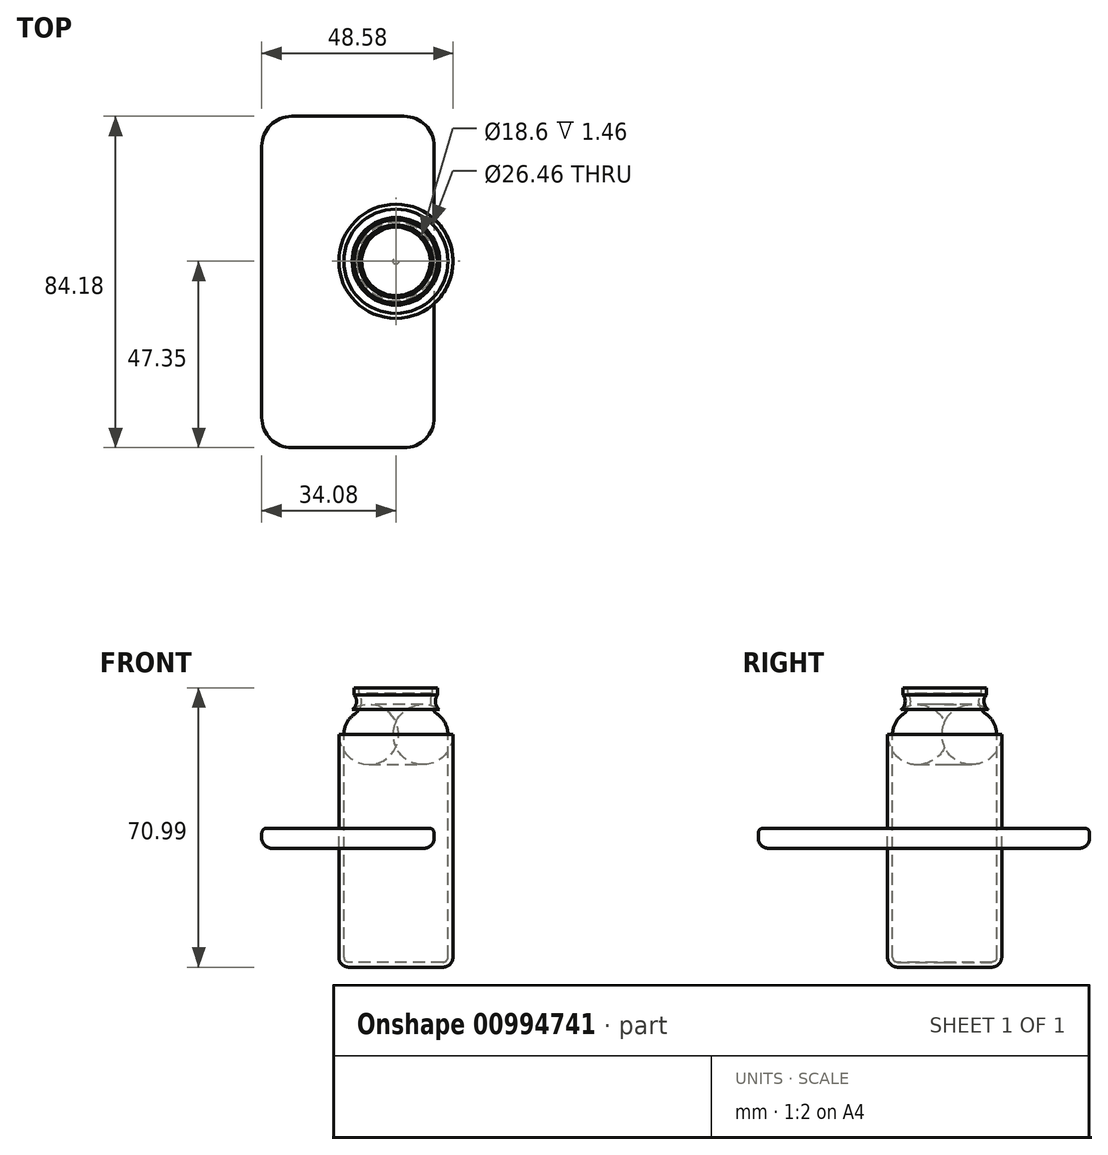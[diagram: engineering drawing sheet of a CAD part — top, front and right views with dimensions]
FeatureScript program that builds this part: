
annotation { "Feature Type Name" : "Feature", "Feature Type Description" : "" }
export const myFeature = defineFeature(function(context is Context, id is Id, definition is map)
    precondition{}
    {
        {
            var Q0;
            Q0=qCreatedBy(makeId("Top.planeOp"),FACE);
            var sketch = newSketch(context, id + "F0", { "sketchPlane" : qUnion([Q0])});
            skLineSegment(sketch, "E0.bottom", {"start": v(-34.08, 36.83) * mm, "end": v(9.72, 36.83) * mm});
            skLineSegment(sketch, "E0.top", {"start": v(-34.08, -47.35) * mm, "end": v(9.72, -47.35) * mm});
            skLineSegment(sketch, "E0.left", {"start": v(-34.08, 36.83) * mm, "end": v(-34.08, -47.35) * mm});
            skLineSegment(sketch, "E0.right", {"start": v(9.72, 36.83) * mm, "end": v(9.72, -47.35) * mm});
            skSolve(sketch);
        }
        {
            var Q0;
            Q0=makeQuery(id+"F0.imprint","IMPRINT",FACE,{"disambiguationData":[TD([[makeQuery(id+"F0.imprint","IMPRINT",EDGE,{"derivedFrom":sQuery(id+"F0.wireOp",EDGE,"E0.bottom")}),-1.0]])]});
            extrude(context, id + "F1", {"entities" : qUnion([Q0]), "depth" : 5.08 * mm, "offsetDistance" : 25.4 * mm});
        }
        {
            var Q0;
            Q0=makeQuery(id+"F1.opExtrude","SWEPT_EDGE",EDGE,{"disambiguationData":[OSD([sQuery(id+"F0.wireOp",EDGE,"E0.top"),sQuery(id+"F0.wireOp",EDGE,"E0.left")])]});
            var Q1;
            Q1=makeQuery(id+"F1.opExtrude","SWEPT_EDGE",EDGE,{"disambiguationData":[OSD([sQuery(id+"F0.wireOp",EDGE,"E0.top"),sQuery(id+"F0.wireOp",EDGE,"E0.right")])]});
            var Q2;
            Q2=makeQuery(id+"F1.opExtrude","SWEPT_EDGE",EDGE,{"disambiguationData":[OSD([sQuery(id+"F0.wireOp",EDGE,"E0.bottom"),sQuery(id+"F0.wireOp",EDGE,"E0.right")])]});
            var Q3;
            Q3=makeQuery(id+"F1.opExtrude","SWEPT_EDGE",EDGE,{"disambiguationData":[OSD([sQuery(id+"F0.wireOp",EDGE,"E0.bottom"),sQuery(id+"F0.wireOp",EDGE,"E0.left")])]});
            fillet(context, id + "F2", {"entities" : qUnion([Q0, Q1, Q2, Q3]), "radius" : 7.62 * mm, "tangentPropagation" : true, "allowEdgeOverflow" : false});
        }
        {
            var Q0;
            Q0=makeQuery(id+"F1.opExtrude","CAP_EDGE",EDGE,{"disambiguationData":[OSD([sQuery(id+"F0.wireOp",EDGE,"E0.left")])],"isStart":true});
            fillet(context, id + "F3", {"entities" : qUnion([Q0]), "radius" : 2.54 * mm, "tangentPropagation" : true, "allowEdgeOverflow" : false});
        }
        {
            var Q0;
            Q0=makeQuery(id+"F1.opExtrude","CAP_EDGE",EDGE,{"disambiguationData":[OSD([sQuery(id+"F0.wireOp",EDGE,"E0.left")])],"isStart":false});
            fillet(context, id + "F4", {"entities" : qUnion([Q0]), "radius" : 1.27 * mm, "tangentPropagation" : true, "allowEdgeOverflow" : false});
        }
        {
            var Q0;
            Q0=qCreatedBy(makeId("Front.planeOp"),FACE);
            var sketch = newSketch(context, id + "F5", { "sketchPlane" : qUnion([Q0])});
            skLineSegment(sketch, "E1.top", {"start": v(0, -30.22) * mm, "end": v(14.5, -30.22) * mm});
            skLineSegment(sketch, "E1.left", {"start": v(0, 32.43) * mm, "end": v(0, -30.22) * mm});
            skLineSegment(sketch, "E1.right", {"start": v(14.5, 33.28) * mm, "end": v(14.5, -30.22) * mm});
            skLineSegment(sketch, "E2", {"start": v(14.5, 33.28) * mm, "end": v(9.09, 36.4) * mm});
            skLineSegment(sketch, "E3", {"start": v(9.09, 36.4) * mm, "end": v(10.57, 38.97) * mm});
            skLineSegment(sketch, "E4", {"start": v(10.57, 38.97) * mm, "end": v(10.57, 40.77) * mm});
            skLineSegment(sketch, "E5", {"start": v(10.57, 40.77) * mm, "end": v(0, 40.77) * mm});
            skLineSegment(sketch, "E6", {"start": v(0, 40.77) * mm, "end": v(0, 32.43) * mm});
            skSolve(sketch);
        }
        {
            var Q0;
            Q0=makeQuery(id+"F5.imprint","IMPRINT",FACE,{"disambiguationData":[TD([[makeQuery(id+"F5.imprint","IMPRINT",EDGE,{"derivedFrom":sQuery(id+"F5.wireOp",EDGE,"E1.top")}),1.0]])]});
            var Q1;
            Q1=sQuery(id+"F5.wireOp",EDGE,"E1.left");
            revolve(context, id + "F6", {"surfaceOperationType" : NewSurfaceOperationType.NEW, "entities" : qUnion([Q0]), "axis" : qUnion([Q1]), "revolveType" : RevolveType.FULL});
        }
        {
            var Q0;
            Q0=makeQuery(id+"F6.opRevolve","SWEPT_EDGE",EDGE,{"disambiguationData":[OSD([sQuery(id+"F5.wireOp",EDGE,"E1.top"),sQuery(id+"F5.wireOp",EDGE,"E1.right")])]});
            fillet(context, id + "F7", {"entities" : qUnion([Q0]), "radius" : 2.54 * mm, "tangentPropagation" : true, "allowEdgeOverflow" : false});
        }
        {
            var Q0;
            Q0=makeQuery(id+"F6.opRevolve","SWEPT_EDGE",EDGE,{"disambiguationData":[OSD([sQuery(id+"F5.wireOp",EDGE,"E1.right"),sQuery(id+"F5.wireOp",EDGE,"E2")])]});
            fillet(context, id + "F8", {"entities" : qUnion([Q0]), "radius" : 7.62 * mm, "tangentPropagation" : true, "allowEdgeOverflow" : false});
        }
        {
            var Q0;
            Q0=makeQuery(id+"F6.opRevolve","SWEPT_EDGE",EDGE,{"disambiguationData":[OSD([sQuery(id+"F5.wireOp",EDGE,"E2"),sQuery(id+"F5.wireOp",EDGE,"E3")])]});
            fillet(context, id + "F9", {"entities" : qUnion([Q0]), "radius" : 2.54 * mm, "tangentPropagation" : true, "allowEdgeOverflow" : false});
        }
        {
            var Q0;
            Q0=makeQuery(id+"F6.opRevolve","SWEPT_FACE",FACE,{"disambiguationData":[OSD([sQuery(id+"F5.wireOp",EDGE,"E5")])]});
            shell(context, id + "F10", {"entities" : qUnion([Q0]), "thickness" : 1.27 * mm});
        }
    });
